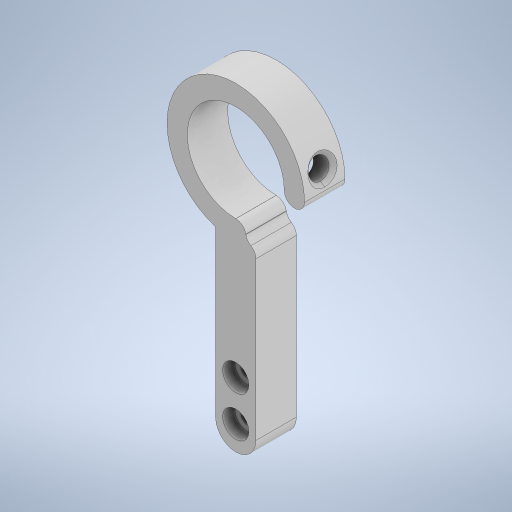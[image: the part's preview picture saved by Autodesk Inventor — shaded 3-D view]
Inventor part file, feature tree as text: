
AUTODESK INVENTOR PART (.ipt)
format: ipt  version: 2023.1 (Build 271208000, 208)  size: 325,632 bytes
history: native  units: mm
features: sketch x4, extrude x3, fillet x2, other x1, revolve x1, chamfer x1
ambient origin geometry x8: Origin, YZ Plane, XZ Plane, XY Plane, X Axis, Y Axis, Z Axis, Center Point
bodies: Body1 (feature_tree)
feature tree (12):
  other  "솔리드1"
  extrude  "돌출1"  Depth=10.0mm
  fillet  "모깎기1"  Radius=50.0mm
  revolve  "회전1"
  chamfer  "모따기1"  Distance=24.0mm
  extrude  "돌출2"  Depth=34.0mm
  fillet  "모깎기2"  Radius=10.0mm
  extrude  "돌출3"  Depth=2.5mm
  sketch  "스케치1"
  sketch  "스케치2"
  sketch  "스케치3"
  sketch  "스케치4"
